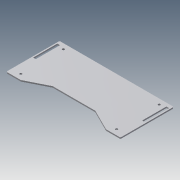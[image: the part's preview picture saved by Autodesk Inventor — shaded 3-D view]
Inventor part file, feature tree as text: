
AUTODESK INVENTOR PART (.ipt)
format: ipt  version: 2014 (Build 180170000, 170)  size: 132,608 bytes
history: native  units: mm
features: extrude x3, sketch x3, fillet x1
ambient origin geometry x8: Origin, YZ Plane, XZ Plane, XY Plane, X Axis, Y Axis, Z Axis, Center Point
bodies: Solid1 (feature_tree)
feature tree (7):
  extrude  "Extrusion1"  Depth=268.0mm
  extrude  "Extrusion2"  Depth=25.0mm
  extrude  "Extrusion5"  Depth=2.0mm
  fillet  "Fillet1"  Radius=3.0mm
  sketch  "Sketch1"  dims[d1=125.0mm d2=268.0mm]
  sketch  "Sketch2"  dims[d4=3.0mm d5=0.0mm d6=25.0mm]
  sketch  "Sketch7"  dims[d7=34.0mm d9=50.0mm d10=3.0mm d11=0.0mm d47=34.0mm d48=21.5mm d49=21.5mm d50=12.5mm d51=12.5mm d56=2.875mm d57=6.25mm d58=2.875mm d59=35.0mm d60=8.0mm d61=5.4mm d62=57.0mm d63=10.0mm d64=0.0mm d65=2.0mm]
